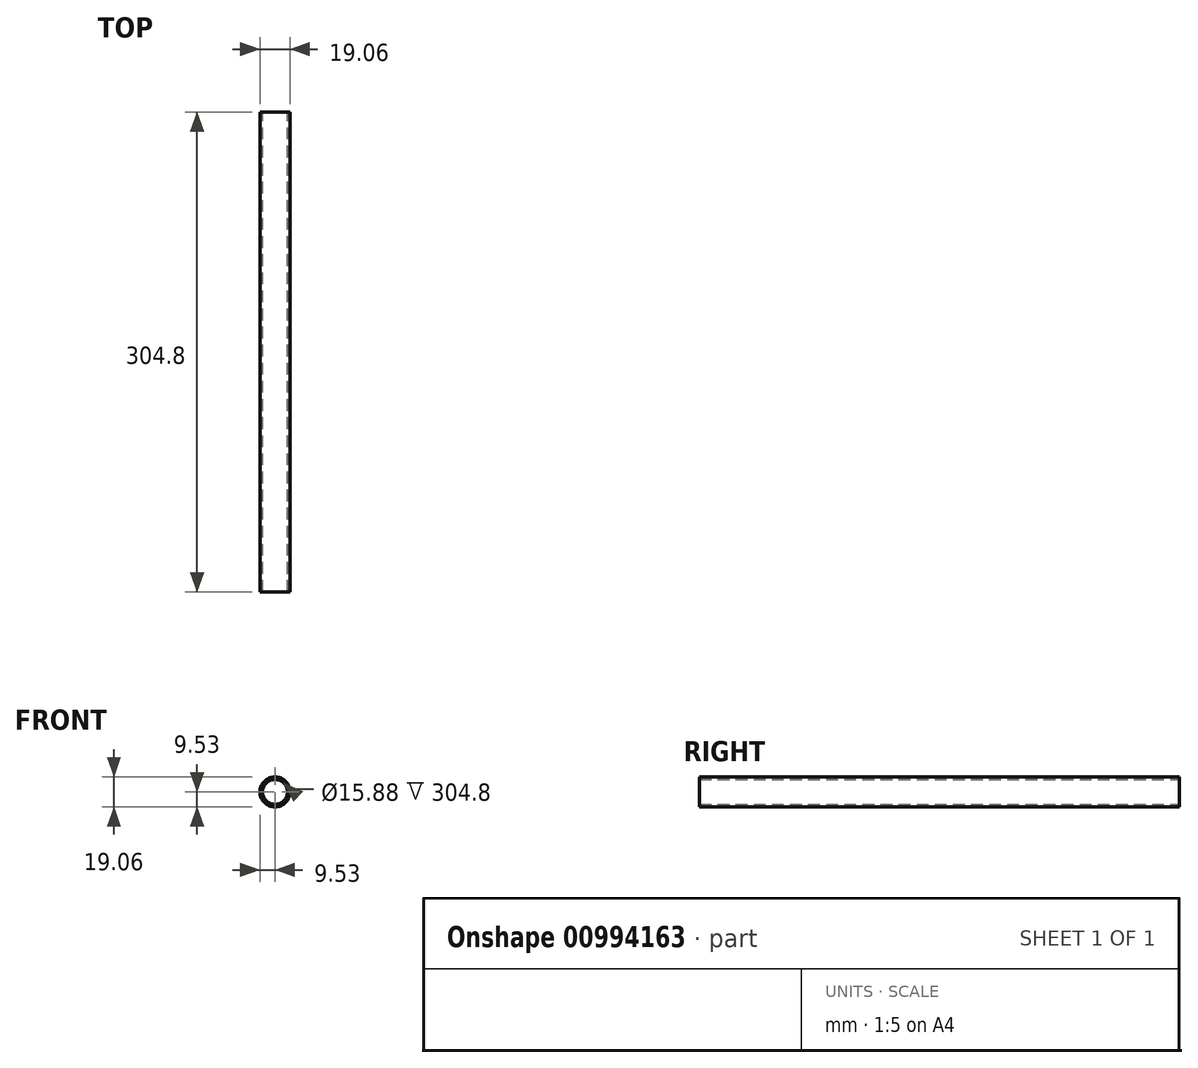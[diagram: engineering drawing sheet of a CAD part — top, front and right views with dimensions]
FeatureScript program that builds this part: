
annotation { "Feature Type Name" : "Feature", "Feature Type Description" : "" }
export const myFeature = defineFeature(function(context is Context, id is Id, definition is map)
    precondition{}
    {
        {
            var Q0;
            Q0=qCreatedBy(makeId("Front.planeOp"),FACE);
            var sketch = newSketch(context, id + "F0", { "sketchPlane" : qUnion([Q0])});
            skCircle(sketch, "E0", {"center": v(0, 0) * mm, "radius": 9.53 * mm});
            skCircle(sketch, "E1", {"center": v(0, 0) * mm, "radius": 7.94 * mm});
            skSolve(sketch);
        }
        {
            var Q0;
            Q0=qSketchRegion(id+"F0",true);
            extrude(context, id + "F1", {"entities" : qUnion([Q0]), "depth" : 304.8 * mm, "offsetDistance" : 25.4 * mm});
        }
    });
